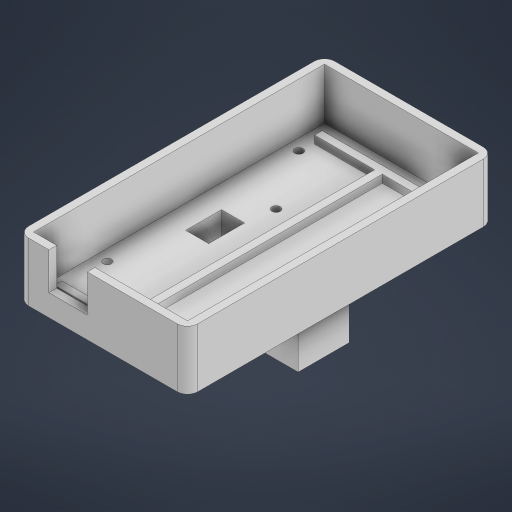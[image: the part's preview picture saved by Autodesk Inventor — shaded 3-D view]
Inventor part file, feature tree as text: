
AUTODESK INVENTOR PART (.ipt)
format: ipt  version: 2024 (Build 280153000, 153)  size: 348,672 bytes
history: native  units: mm
features: other x10, reference x10, sketch x8, extrude x8, fillet x1
ambient origin geometry x8: Origin, YZ Plane, XZ Plane, XY Plane, X Axis, Y Axis, Z Axis, Center Point
bodies: Body1 (feature_tree)
feature tree (37):
  other  "Твердое тело1"
  sketch  "Эскиз1"
  other  "РабПлоскость1"
  extrude  "Выдавливание1"  Depth=15.0mm
  extrude  "Выдавливание2"  Depth=15.0mm
  extrude  "Выдавливание3"  Depth=3.0mm
  extrude  "Выдавливание4"  Depth=10.0mm TaperAngle=0.0deg
  fillet  "Сопряжение3"  Radius=3.0mm
  extrude  "Выдавливание5"  Depth=3.0mm
  extrude  "Выдавливание6"  Depth=3.0mm
  other  "Непосредственное редактирование1"
  extrude  "Выдавливание7"  Depth=17.0mm TaperAngle=0.0deg
  extrude  "Выдавливание9"  Depth=3.0mm TaperAngle=0.0deg
  reference  "Ссылка1"
  reference  "Ссылка2"
  reference  "Ссылка3"
  reference  "Ссылка4"
  sketch  "Эскиз2"
  sketch  "Эскиз3"
  sketch  "Эскиз4"
  sketch  "Эскиз9"
  sketch  "Эскиз10"
  reference  "Ссылка5"
  reference  "Ссылка6"
  reference  "Ссылка7"
  reference  "Ссылка8"
  reference  "Ссылка9"
  reference  "Ссылка10"
  sketch  "Эскиз11"
  sketch  "Эскиз13"
  parser-record x1  (decoder bookkeeping rows leaked as tree rows — omitted from the tree; the rows remain in map.json)
  other  "main_assembly.iam"
  other  "base_assembly:1"
  other  "section:4"
  other  "main axis:1"
  other  "Arduino MEGA 2560 R3:1"
  other  "Перенос1"
note: 1 file-system path scrubbed to <path> (originals preserved in map.json)
